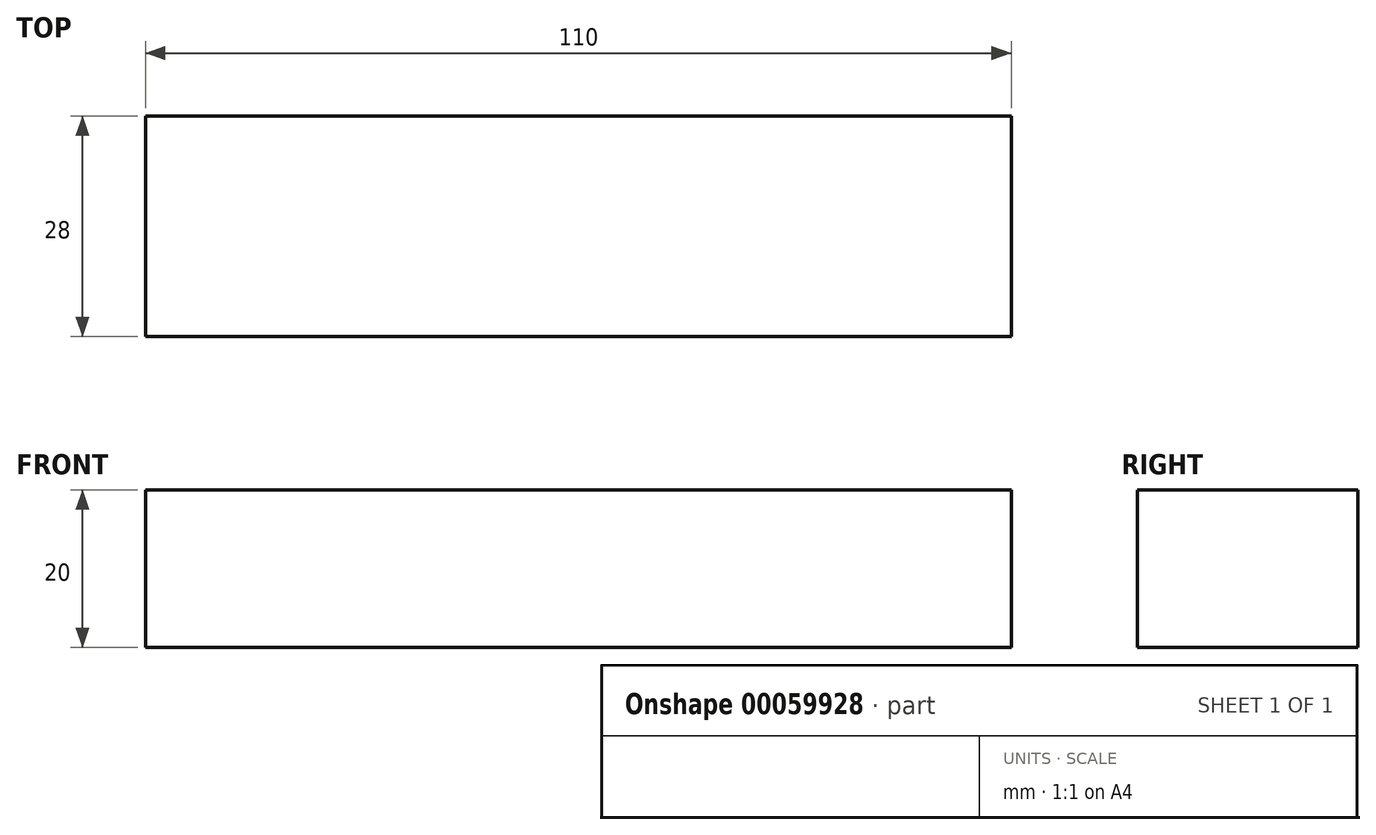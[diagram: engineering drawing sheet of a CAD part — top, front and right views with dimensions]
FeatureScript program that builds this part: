
annotation { "Feature Type Name" : "Feature", "Feature Type Description" : "" }
export const myFeature = defineFeature(function(context is Context, id is Id, definition is map)
    precondition{}
    {
        {
            var Q0;
            Q0=qCreatedBy(makeId("Top.planeOp"),FACE);
            var sketch = newSketch(context, id + "F0", { "sketchPlane" : qUnion([Q0])});
            skLineSegment(sketch, "E0.bottom", {"start": v(0, 0) * mm, "end": v(110, 0) * mm});
            skLineSegment(sketch, "E0.top", {"start": v(0, 28) * mm, "end": v(110, 28) * mm});
            skLineSegment(sketch, "E0.left", {"start": v(0, 0) * mm, "end": v(0, 28) * mm});
            skLineSegment(sketch, "E0.right", {"start": v(110, 0) * mm, "end": v(110, 28) * mm});
            skSolve(sketch);
        }
        {
            var Q0;
            Q0=makeQuery(id+"F0.imprint","IMPRINT",FACE,{"disambiguationData":[TD([[makeQuery(id+"F0.imprint","IMPRINT",EDGE,{"derivedFrom":sQuery(id+"F0.wireOp",EDGE,"E0.bottom")}),1.0]])]});
            extrude(context, id + "F1", {"entities" : qUnion([Q0]), "depth" : 20 * mm});
        }
    });
